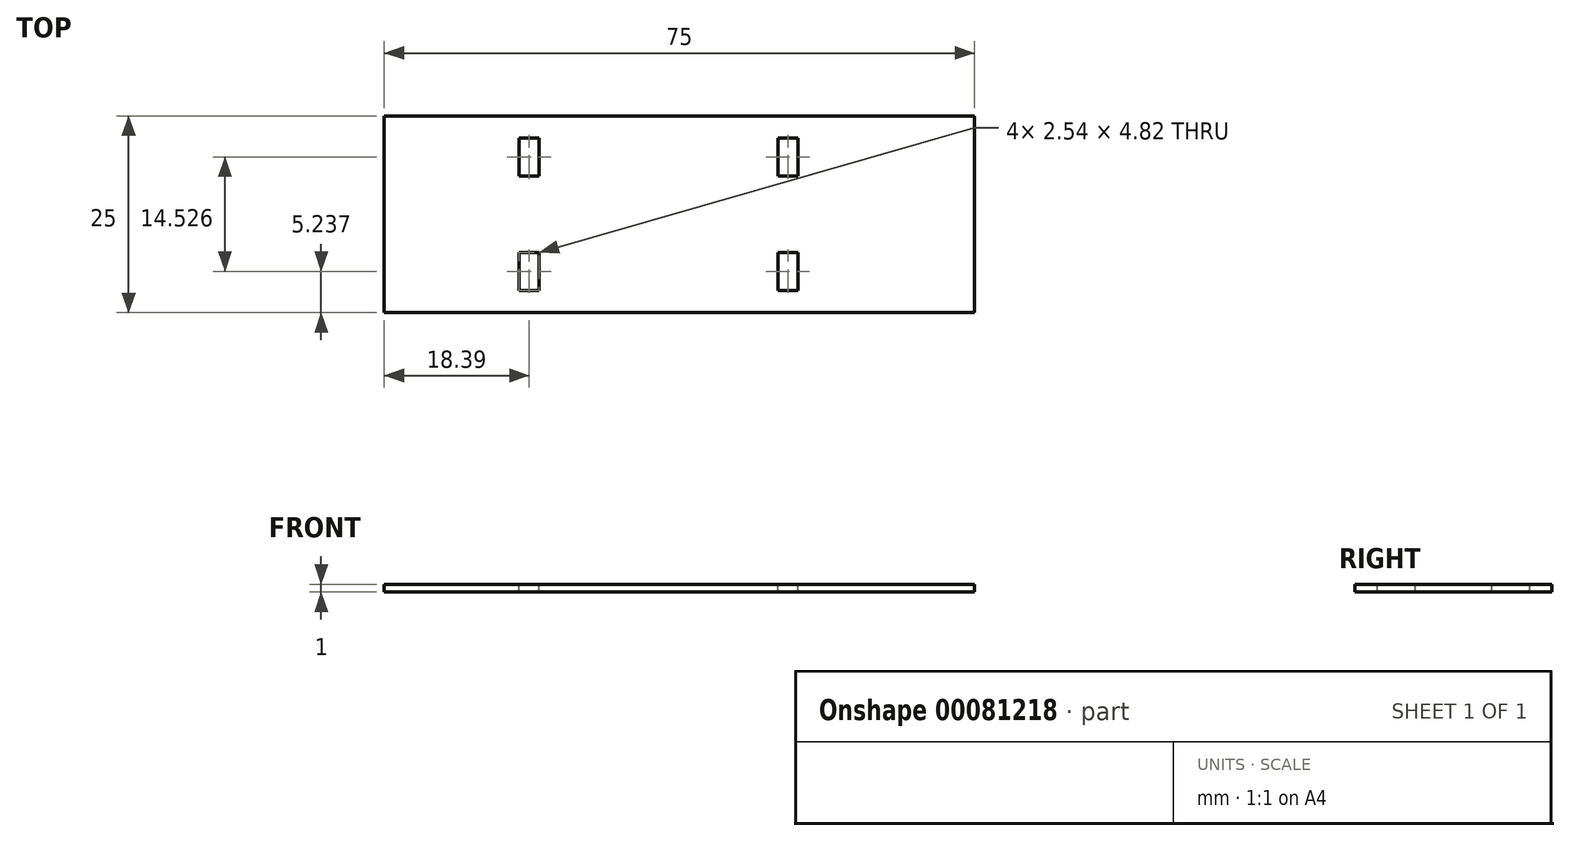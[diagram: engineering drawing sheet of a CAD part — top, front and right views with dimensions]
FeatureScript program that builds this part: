
annotation { "Feature Type Name" : "Feature", "Feature Type Description" : "" }
export const myFeature = defineFeature(function(context is Context, id is Id, definition is map)
    precondition{}
    {
        {
            var Q0;
            Q0=qCreatedBy(makeId("Top.planeOp"),FACE);
            var sketch = newSketch(context, id + "F0", { "sketchPlane" : qUnion([Q0])});
            skLineSegment(sketch, "E0.bottom", {"start": v(-37.5, 12.5) * mm, "end": v(37.5, 12.5) * mm});
            skLineSegment(sketch, "E0.top", {"start": v(-37.5, -12.5) * mm, "end": v(37.5, -12.5) * mm});
            skLineSegment(sketch, "E0.left", {"start": v(-37.5, 12.5) * mm, "end": v(-37.5, -12.5) * mm});
            skLineSegment(sketch, "E0.right", {"start": v(37.5, 12.5) * mm, "end": v(37.5, -12.5) * mm});
            skPoint(sketch, "E0.middle", {"position": v(0, 0) * mm});
            skSolve(sketch);
        }
        {
            var Q0;
            Q0 = qSketchRegion(id + "F0", true);
            extrude(context, id + "F1", {"entities" : qUnion([Q0]), "depth" : 1 * mm});
        }
        {
            var Q0;
            Q0=makeQuery(id+"F1.opExtrude","CAP_FACE",FACE,{"disambiguationData":[OSD([sQuery(id+"F0.wireOp",EDGE,"E0.bottom"),sQuery(id+"F0.wireOp",EDGE,"E0.top"),sQuery(id+"F0.wireOp",EDGE,"E0.left"),sQuery(id+"F0.wireOp",EDGE,"E0.right")])],"isStart":false});
            var sketch = newSketch(context, id + "F2", { "sketchPlane" : qUnion([Q0])});
            skLineSegment(sketch, "E1.MirrorCS", {"start": v(12.5, -9.68) * mm, "end": v(12.5, -4.85) * mm});
            skLineSegment(sketch, "E2", {"start": v(-17.84, 9.68) * mm, "end": v(-17.84, 4.85) * mm});
            skLineSegment(sketch, "E3.bottom", {"start": v(-17.84, 4.85) * mm, "end": v(-20.38, 4.85) * mm});
            skLineSegment(sketch, "E3.top", {"start": v(-17.84, 9.68) * mm, "end": v(-20.38, 9.68) * mm});
            skLineSegment(sketch, "E3.left", {"start": v(-17.84, 4.85) * mm, "end": v(-17.84, 9.68) * mm});
            skLineSegment(sketch, "E3.right", {"start": v(-20.38, 4.85) * mm, "end": v(-20.38, 9.68) * mm});
            skLineSegment(sketch, "E4.bottom", {"start": v(12.5, -4.85) * mm, "end": v(15.05, -4.85) * mm});
            skLineSegment(sketch, "E4.top", {"start": v(12.5, -9.68) * mm, "end": v(15.05, -9.68) * mm});
            skLineSegment(sketch, "E4.left", {"start": v(12.5, -4.85) * mm, "end": v(12.5, -9.68) * mm});
            skLineSegment(sketch, "E4.right", {"start": v(15.05, -4.85) * mm, "end": v(15.05, -9.68) * mm});
            skLineSegment(sketch, "E5.MirrorCS", {"start": v(-17.84, -4.85) * mm, "end": v(-20.38, -4.85) * mm});
            skLineSegment(sketch, "E6.MirrorCS", {"start": v(-20.38, -4.85) * mm, "end": v(-20.38, -9.68) * mm});
            skLineSegment(sketch, "E7.MirrorCS", {"start": v(-17.84, -9.68) * mm, "end": v(-20.38, -9.68) * mm});
            skLineSegment(sketch, "E8.MirrorCS", {"start": v(-17.84, -4.85) * mm, "end": v(-17.84, -9.68) * mm});
            skLineSegment(sketch, "E9.MirrorCS", {"start": v(12.5, 9.68) * mm, "end": v(12.5, 4.85) * mm});
            skLineSegment(sketch, "E10.MirrorCS", {"start": v(12.5, 4.85) * mm, "end": v(15.05, 4.85) * mm});
            skLineSegment(sketch, "E11.MirrorCS", {"start": v(15.05, 4.85) * mm, "end": v(15.05, 9.68) * mm});
            skLineSegment(sketch, "E12.MirrorCS", {"start": v(12.5, 9.68) * mm, "end": v(15.05, 9.68) * mm});
            skSolve(sketch);
        }
        {
            var Q0;
            Q0 = qSketchRegion(id + "F2", true);
            extrude(context, id + "F3", {"entities" : qUnion([Q0]), "operationType" : NewBodyOperationType.REMOVE, "oppositeDirection" : true, "depth" : 25.4 * mm});
        }
    });
